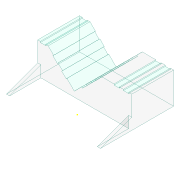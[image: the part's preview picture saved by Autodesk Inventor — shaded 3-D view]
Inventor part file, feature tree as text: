
AUTODESK INVENTOR PART (.ipt)
format: ipt  version: 2022 (Build 260153000, 153)  size: 175,104 bytes
history: native  units: mm
features: sketch x5, extrude x4, projected_geometry x3
ambient origin geometry x8: Origin, YZ Plane, XZ Plane, XY Plane, X Axis, Y Axis, Z Axis, Center Point
bodies: Solid1 (feature_tree)
feature tree (12):
  extrude  "Extrusion1"  Depth=150.0mm
  sketch  "Sketch2"  dims[d2=150.0mm d3=175.0mm]
  extrude  "Extrusion2"  Depth=150.0mm
  extrude  "Extrusion3"  Depth=200.0mm TaperAngle=0.0deg
  extrude  "Extrusion4"  Depth=15.0mm TaperAngle=0.0deg
  sketch  "Sketch1"  dims[d0=350.0mm d1=150.0mm]
  sketch  "Sketch3"  dims[d5=100.0mm d6=200.0mm d7=0.0mm]
  projected_geometry  "Projected Loop1"
  sketch  "Sketch4"  dims[d8=15.0mm d9=0.0mm d10=15.0mm d11=0.0mm]
  projected_geometry  "Projected Loop2"
  sketch  "Sketch5"  dims[d12=3.490659mm d13=150.0mm d16=90.0deg d17=50.0mm d18=50.0mm d19=5.0mm d20=30.0mm d21=5.0mm d22=30.0mm d23=50.0mm d24=30.0mm d25=10.0mm d26=0.0mm d27=5.0mm d28=25.0mm d29=25.0mm d30=20.0mm d31=15.0mm d32=25.0mm d33=12.5mm d34=5.0mm]
  projected_geometry  "Projected Loop3"
